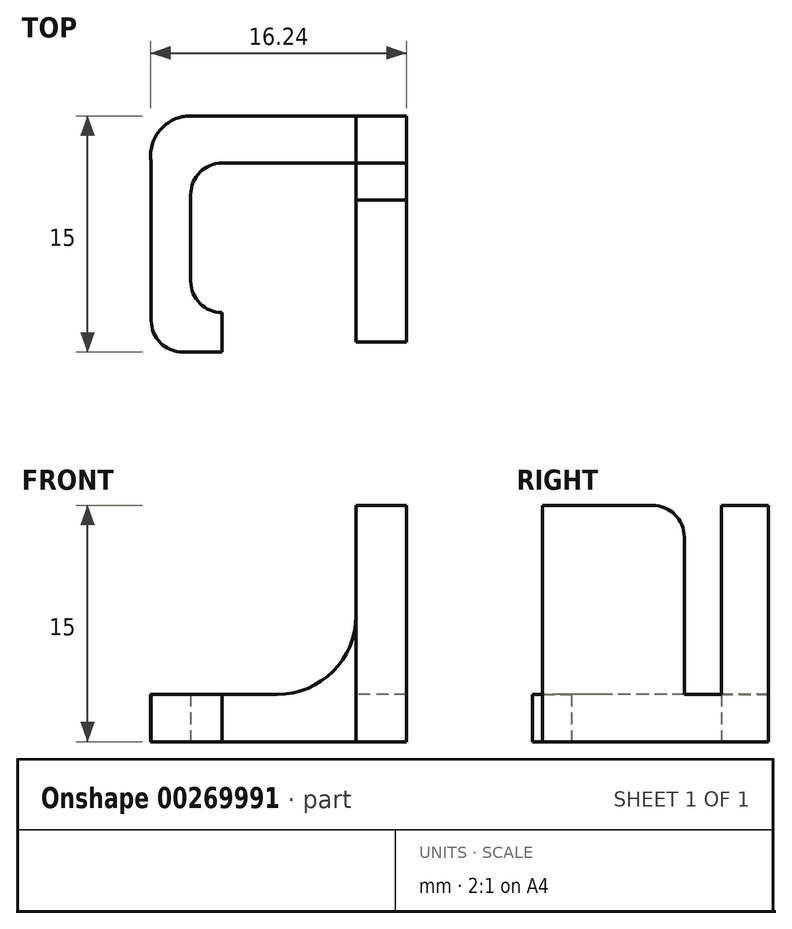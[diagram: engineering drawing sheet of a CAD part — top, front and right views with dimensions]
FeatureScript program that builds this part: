
annotation { "Feature Type Name" : "Feature", "Feature Type Description" : "" }
export const myFeature = defineFeature(function(context is Context, id is Id, definition is map)
    precondition{}
    {
        {
            var Q0;
            Q0=qCreatedBy(makeId("Top.planeOp"),FACE);
            var sketch = newSketch(context, id + "F0", { "sketchPlane" : qUnion([Q0])});
            skLineSegment(sketch, "E0.bottom", {"start": v(0, 0) * mm, "end": v(-3.2, 0) * mm});
            skLineSegment(sketch, "E0.top", {"start": v(0, 9) * mm, "end": v(-3.2, 9) * mm});
            skLineSegment(sketch, "E0.left", {"start": v(0, 0) * mm, "end": v(0, 9) * mm});
            skLineSegment(sketch, "E0.right", {"start": v(-3.2, 0) * mm, "end": v(-3.2, 9) * mm});
            skLineSegment(sketch, "E1.bottom", {"start": v(-3.2, 9) * mm, "end": v(0, 9) * mm});
            skLineSegment(sketch, "E1.top", {"start": v(-3.2, 11.35) * mm, "end": v(0, 11.35) * mm});
            skLineSegment(sketch, "E1.left", {"start": v(-3.2, 9) * mm, "end": v(-3.2, 11.35) * mm});
            skLineSegment(sketch, "E1.right", {"start": v(0, 9) * mm, "end": v(0, 11.35) * mm});
            skLineSegment(sketch, "E2.top", {"start": v(-3.2, 14.35) * mm, "end": v(0, 14.35) * mm});
            skLineSegment(sketch, "E2.left", {"start": v(-3.2, 11.35) * mm, "end": v(-3.2, 14.35) * mm});
            skLineSegment(sketch, "E2.right", {"start": v(0, 11.35) * mm, "end": v(0, 14.35) * mm});
            skLineSegment(sketch, "E3.bottom", {"start": v(-3.2, 14.35) * mm, "end": v(-13.7, 14.35) * mm});
            skLineSegment(sketch, "E3.top", {"start": v(-3.2, 11.35) * mm, "end": v(-13.7, 11.35) * mm});
            skLineSegment(sketch, "E3.left", {"start": v(-3.2, 14.35) * mm, "end": v(-3.2, 11.35) * mm});
            skLineSegment(sketch, "E3.right", {"start": v(-13.7, 11.8) * mm, "end": v(-13.7, 11.35) * mm});
            skLineSegment(sketch, "E4.top", {"start": v(-13.7, -0.65) * mm, "end": v(-16.2, -0.65) * mm});
            skLineSegment(sketch, "E4.left", {"start": v(-13.7, 11.35) * mm, "end": v(-13.7, 1.85) * mm});
            skLineSegment(sketch, "E4.right", {"start": v(-16.2, 11.35) * mm, "end": v(-16.2, -0.65) * mm});
            skArc(sketch, "E5", {"start": v(-13.7, 14.35) * mm, "mid": v(-15.65, 13.44) * mm, "end": v(-16.2, 11.35) * mm});
            skLineSegment(sketch, "E6.bottom", {"start": v(-13.7, -0.65) * mm, "end": v(-11.7, -0.65) * mm});
            skLineSegment(sketch, "E6.top", {"start": v(-13.7, 1.85) * mm, "end": v(-11.7, 1.85) * mm});
            skLineSegment(sketch, "E6.right", {"start": v(-11.7, -0.65) * mm, "end": v(-11.7, 1.85) * mm});
            skSolve(sketch);
        }
        {
            var Q0;
            Q0=makeQuery(id+"F0.imprint","IMPRINT",FACE,{"disambiguationData":[TD([[makeQuery(id+"F0.imprint","IMPRINT",EDGE,{"derivedFrom":sQuery(id+"F0.wireOp",EDGE,"E0.bottom")}),-1.0]])]});
            var Q1;
            Q1=makeQuery(id+"F0.imprint","IMPRINT",FACE,{"disambiguationData":[TD([[makeQuery(id+"F0.imprint","IMPRINT",EDGE,{"derivedFrom":sQuery(id+"F0.wireOp",EDGE,"E1.top")}),1.0]])]});
            extrude(context, id + "F1", {"entities" : qUnion([Q0, Q1]), "depth" : 15 * mm, "offsetDistance" : 25 * mm});
        }
        {
            var Q0;
            Q0=makeQuery(id+"F0.imprint","IMPRINT",FACE,{"disambiguationData":[TD([[makeQuery(id+"F0.imprint","IMPRINT",EDGE,{"derivedFrom":sQuery(id+"F0.wireOp",EDGE,"E0.top")}),-1.0]])]});
            var Q1;
            Q1=makeQuery(id+"F0.imprint","IMPRINT",FACE,{"disambiguationData":[TD([[makeQuery(id+"F0.imprint","IMPRINT",EDGE,{"derivedFrom":sQuery(id+"F0.wireOp",EDGE,"E2.left")}),1.0]])]});
            extrude(context, id + "F2", {"entities" : qUnion([Q0, Q1]), "operationType" : NewBodyOperationType.ADD, "depth" : 3 * mm, "offsetDistance" : 25 * mm});
        }
        {
            var Q0;
            Q0=makeQuery(id+"F1.opExtrude","CAP_EDGE",EDGE,{"disambiguationData":[OSD([sQuery(id+"F0.wireOp",EDGE,"E0.top")])],"isStart":false});
            fillet(context, id + "F3", {"entities" : qUnion([Q0]), "tangentPropagation" : true, "radius" : 2 * mm, "defaultsChanged" : true, "vertexSettings" : [], "allowEdgeOverflow" : false});
        }
        {
            var Q0;
            Q0=makeQuery(id+"F2.opExtrude","SWEPT_EDGE",EDGE,{"disambiguationData":[OSD([sQuery(id+"F0.wireOp",EDGE,"E4.top"),sQuery(id+"F0.wireOp",EDGE,"E4.right")])]});
            var Q1;
            Q1=makeQuery(id+"F2.opExtrude","SWEPT_EDGE",EDGE,{"disambiguationData":[OSD([sQuery(id+"F0.wireOp",EDGE,"E3.top"),sQuery(id+"F0.wireOp",EDGE,"E4.left")])]});
            var Q2;
            Q2=makeQuery(id+"F2.opExtrude","SWEPT_EDGE",EDGE,{"disambiguationData":[OSD([sQuery(id+"F0.wireOp",EDGE,"E4.left"),sQuery(id+"F0.wireOp",EDGE,"E6.top")])]});
            fillet(context, id + "F4", {"entities" : qUnion([Q0, Q1, Q2]), "tangentPropagation" : true, "radius" : 2 * mm, "defaultsChanged" : false, "vertexSettings" : [], "allowEdgeOverflow" : false});
        }
        {
            var Q0;
            Q0=makeQuery(id+"F2.opExtrude","CAP_EDGE",EDGE,{"disambiguationData":[OSD([sQuery(id+"F0.wireOp",EDGE,"E2.left")])],"isStart":false});
            fillet(context, id + "F5", {"entities" : qUnion([Q0]), "tangentPropagation" : true, "radius" : 5 * mm, "defaultsChanged" : false, "vertexSettings" : [], "allowEdgeOverflow" : false});
        }
    });
